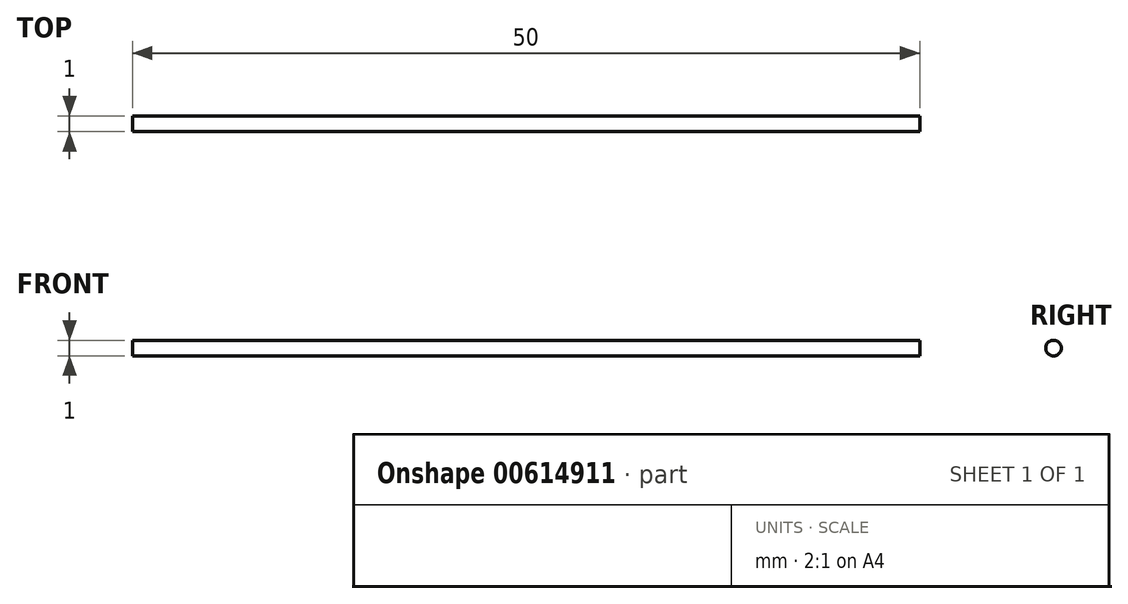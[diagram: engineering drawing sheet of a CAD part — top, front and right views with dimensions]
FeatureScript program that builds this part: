
annotation { "Feature Type Name" : "Feature", "Feature Type Description" : "" }
export const myFeature = defineFeature(function(context is Context, id is Id, definition is map)
    precondition{}
    {
        {
            var Q0;
            Q0=qCreatedBy(makeId("Right.planeOp"),FACE);
            var sketch = newSketch(context, id + "F0", { "sketchPlane" : qUnion([Q0])});
            skCircle(sketch, "E0", {"center": v(0, 0) * mm, "radius": 0.5 * mm});
            skSolve(sketch);
        }
        {
            var Q0;
            Q0 = qSketchRegion(id + "F0", true);
            extrude(context, id + "F1", {"entities" : qUnion([Q0]), "depth" : 50 * mm, "offsetDistance" : 25 * mm});
        }
    });
